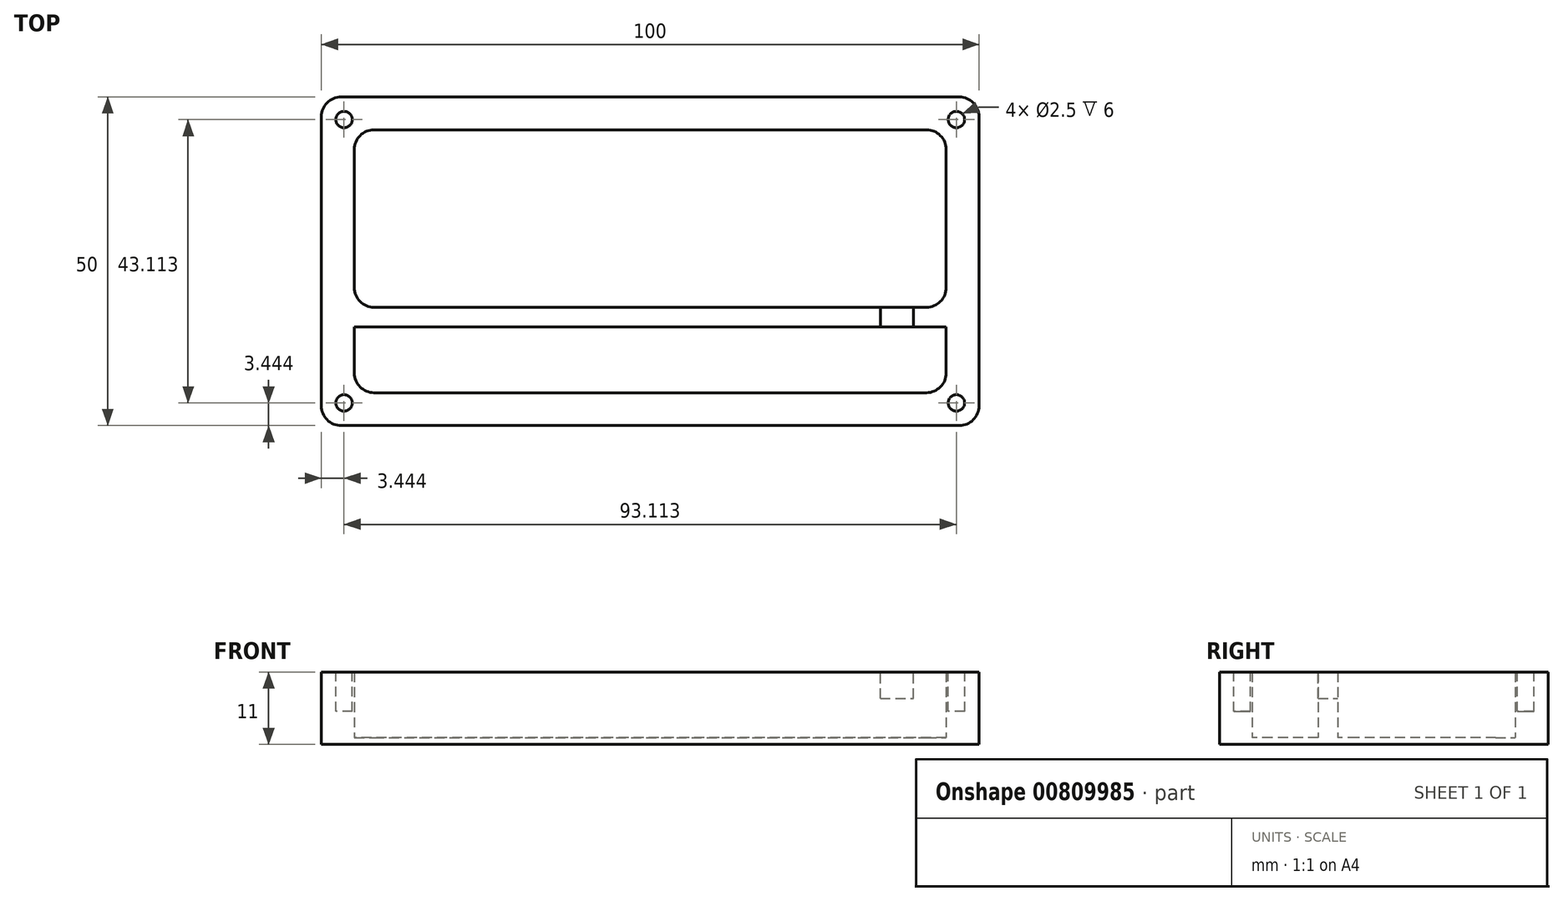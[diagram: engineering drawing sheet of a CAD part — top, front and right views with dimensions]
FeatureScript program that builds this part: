
annotation { "Feature Type Name" : "Feature", "Feature Type Description" : "" }
export const myFeature = defineFeature(function(context is Context, id is Id, definition is map)
    precondition{}
    {
        {
            var Q0;
            Q0=qCreatedBy(makeId("Top.planeOp"),FACE);
            var sketch = newSketch(context, id + "F0", { "sketchPlane" : qUnion([Q0])});
            skLineSegment(sketch, "E0.bottom", {"start": v(-50, -25) * mm, "end": v(50, -25) * mm});
            skLineSegment(sketch, "E0.top", {"start": v(-50, 25) * mm, "end": v(50, 25) * mm});
            skLineSegment(sketch, "E0.left", {"start": v(-50, -25) * mm, "end": v(-50, 25) * mm});
            skLineSegment(sketch, "E0.right", {"start": v(50, -25) * mm, "end": v(50, 25) * mm});
            skLineSegment(sketch, "E1", {"start": v(0, -25) * mm, "end": v(0, 74.13) * mm, "construction": true});
            skLineSegment(sketch, "E2", {"start": v(-150.25, 0) * mm, "end": v(50, 0) * mm, "construction": true});
            skSolve(sketch);
        }
        {
            var Q0;
            Q0 = qSketchRegion(id + "F0", true);
            extrude(context, id + "F1", {"entities" : qUnion([Q0]), "depth" : 1 * mm, "offsetDistance" : 25 * mm});
        }
        {
            var Q0;
            Q0=makeQuery(id+"F1.opExtrude","CAP_FACE",FACE,{"disambiguationData":[OSD([sQuery(id+"F0.wireOp",EDGE,"E0.bottom"),sQuery(id+"F0.wireOp",EDGE,"E0.top"),sQuery(id+"F0.wireOp",EDGE,"E0.left"),sQuery(id+"F0.wireOp",EDGE,"E0.right")])],"isStart":false});
            var sketch = newSketch(context, id + "F2", { "sketchPlane" : qUnion([Q0])});
            skLineSegment(sketch, "E3.bottom", {"start": v(-50, 25) * mm, "end": v(50, 25) * mm});
            skLineSegment(sketch, "E3.top", {"start": v(-50, -25) * mm, "end": v(50, -25) * mm});
            skLineSegment(sketch, "E3.left", {"start": v(-50, 25) * mm, "end": v(-50, -25) * mm});
            skLineSegment(sketch, "E3.right", {"start": v(50, 25) * mm, "end": v(50, -25) * mm});
            skLineSegment(sketch, "E4.bottom", {"start": v(-45, 20) * mm, "end": v(45, 20) * mm});
            skLineSegment(sketch, "E4.top", {"start": v(-45, -20) * mm, "end": v(45, -20) * mm});
            skLineSegment(sketch, "E4.left", {"start": v(-45, 20) * mm, "end": v(-45, -20) * mm});
            skLineSegment(sketch, "E4.right", {"start": v(45, 20) * mm, "end": v(45, -20) * mm});
            skSolve(sketch);
        }
        {
            var Q0;
            Q0=makeQuery(id+"F2.imprint","IMPRINT",FACE,{"disambiguationData":[TD([[makeQuery(id+"F2.imprint","IMPRINT",EDGE,{"derivedFrom":sQuery(id+"F2.wireOp",EDGE,"E3.bottom")}),-1.0]])]});
            var Q1;
            Q1 = qSketchRegion(id + "F2", true);
            extrude(context, id + "F3", {"entities" : qUnion([Q0, Q1]), "operationType" : NewBodyOperationType.ADD, "depth" : 10 * mm, "offsetDistance" : 25 * mm});
        }
        {
            var Q0;
            Q0=qCreatedBy(makeId("Top.planeOp"),FACE);
            var sketch = newSketch(context, id + "F4", { "sketchPlane" : qUnion([Q0])});
            skLineSegment(sketch, "E5.bottom", {"start": v(-45, -7) * mm, "end": v(45, -7) * mm});
            skLineSegment(sketch, "E5.top", {"start": v(-45, -10) * mm, "end": v(45, -10) * mm});
            skLineSegment(sketch, "E5.right", {"start": v(45, -7) * mm, "end": v(45, -10) * mm});
            skLineSegment(sketch, "E6", {"start": v(-45, -7) * mm, "end": v(-45, -10) * mm});
            skSolve(sketch);
        }
        {
            var Q0;
            Q0 = qSketchRegion(id + "F4", true);
            var Q1;
            Q1=makeQuery(id+"F3.opExtrude","CAP_FACE",FACE,{"disambiguationData":[OSD([sQuery(id+"F2.wireOp",EDGE,"E3.bottom"),sQuery(id+"F2.wireOp",EDGE,"E3.top"),sQuery(id+"F2.wireOp",EDGE,"E3.left"),sQuery(id+"F2.wireOp",EDGE,"E3.right"),sQuery(id+"F2.wireOp",EDGE,"E4.bottom"),sQuery(id+"F2.wireOp",EDGE,"E4.top"),sQuery(id+"F2.wireOp",EDGE,"E4.left"),sQuery(id+"F2.wireOp",EDGE,"E4.right")])],"isStart":false});
            extrude(context, id + "F5", {"entities" : qUnion([Q0]), "operationType" : NewBodyOperationType.ADD, "endBound" : BoundingType.UP_TO_SURFACE, "depth" : 25 * mm, "endBoundEntityFace" : qUnion([Q1]), "offsetDistance" : 25 * mm});
        }
        {
            var Q0;
            Q0=makeQuery(id+"F5.opExtrude","SWEPT_FACE",FACE,{"disambiguationData":[OSD([sQuery(id+"F4.wireOp",EDGE,"E5.bottom")])]});
            var sketch = newSketch(context, id + "F6", { "sketchPlane" : qUnion([Q0])});
            skLineSegment(sketch, "E7.bottom", {"start": v(-40, 11) * mm, "end": v(-35, 11) * mm});
            skLineSegment(sketch, "E7.top", {"start": v(-40, 7) * mm, "end": v(-35, 7) * mm});
            skLineSegment(sketch, "E7.left", {"start": v(-40, 11) * mm, "end": v(-40, 7) * mm});
            skLineSegment(sketch, "E7.right", {"start": v(-35, 11) * mm, "end": v(-35, 7) * mm});
            skSolve(sketch);
        }
        {
            var Q0;
            Q0 = qSketchRegion(id + "F6", true);
            extrude(context, id + "F7", {"entities" : qUnion([Q0]), "operationType" : NewBodyOperationType.REMOVE, "endBound" : BoundingType.UP_TO_NEXT, "oppositeDirection" : true, "depth" : 25 * mm, "offsetDistance" : 25 * mm});
        }
        {
            var Q0;
            Q0=makeQuery(id+"F3.boolean.opBoolean","MERGE",EDGE,{"derivedFrom":[makeQuery(id+"F1.opExtrude","SWEPT_EDGE",EDGE,{"disambiguationData":[OSD([sQuery(id+"F0.wireOp",EDGE,"E0.bottom"),sQuery(id+"F0.wireOp",EDGE,"E0.right")])]}),makeQuery(id+"F3.opExtrude","SWEPT_EDGE",EDGE,{"disambiguationData":[OSD([sQuery(id+"F2.wireOp",EDGE,"E3.top"),sQuery(id+"F2.wireOp",EDGE,"E3.right")])]})]});
            var Q1;
            Q1=makeQuery(id+"F3.boolean.opBoolean","MERGE",EDGE,{"derivedFrom":[makeQuery(id+"F1.opExtrude","SWEPT_EDGE",EDGE,{"disambiguationData":[OSD([sQuery(id+"F0.wireOp",EDGE,"E0.top"),sQuery(id+"F0.wireOp",EDGE,"E0.right")])]}),makeQuery(id+"F3.opExtrude","SWEPT_EDGE",EDGE,{"disambiguationData":[OSD([sQuery(id+"F2.wireOp",EDGE,"E3.bottom"),sQuery(id+"F2.wireOp",EDGE,"E3.right")])]})]});
            var Q2;
            Q2=makeQuery(id+"F3.boolean.opBoolean","MERGE",EDGE,{"derivedFrom":[makeQuery(id+"F1.opExtrude","SWEPT_EDGE",EDGE,{"disambiguationData":[OSD([sQuery(id+"F0.wireOp",EDGE,"E0.bottom"),sQuery(id+"F0.wireOp",EDGE,"E0.left")])]}),makeQuery(id+"F3.opExtrude","SWEPT_EDGE",EDGE,{"disambiguationData":[OSD([sQuery(id+"F2.wireOp",EDGE,"E3.top"),sQuery(id+"F2.wireOp",EDGE,"E3.left")])]})]});
            var Q3;
            Q3=makeQuery(id+"F3.boolean.opBoolean","MERGE",EDGE,{"derivedFrom":[makeQuery(id+"F1.opExtrude","SWEPT_EDGE",EDGE,{"disambiguationData":[OSD([sQuery(id+"F0.wireOp",EDGE,"E0.top"),sQuery(id+"F0.wireOp",EDGE,"E0.left")])]}),makeQuery(id+"F3.opExtrude","SWEPT_EDGE",EDGE,{"disambiguationData":[OSD([sQuery(id+"F2.wireOp",EDGE,"E3.bottom"),sQuery(id+"F2.wireOp",EDGE,"E3.left")])]})]});
            var Q4;
            Q4=makeQuery(id+"F3.opExtrude","SWEPT_EDGE",EDGE,{"disambiguationData":[OSD([sQuery(id+"F2.wireOp",EDGE,"E4.top"),sQuery(id+"F2.wireOp",EDGE,"E4.right")])]});
            var Q5;
            Q5=makeQuery(id+"F3.opExtrude","SWEPT_EDGE",EDGE,{"disambiguationData":[OSD([sQuery(id+"F2.wireOp",EDGE,"E4.top"),sQuery(id+"F2.wireOp",EDGE,"E4.left")])]});
            var Q6;
            Q6=makeQuery(id+"F3.opExtrude","SWEPT_EDGE",EDGE,{"disambiguationData":[OSD([sQuery(id+"F2.wireOp",EDGE,"E4.bottom"),sQuery(id+"F2.wireOp",EDGE,"E4.right")])]});
            var Q7;
            Q7=makeQuery(id+"F3.opExtrude","SWEPT_EDGE",EDGE,{"disambiguationData":[OSD([sQuery(id+"F2.wireOp",EDGE,"E4.bottom"),sQuery(id+"F2.wireOp",EDGE,"E4.left")])]});
            var Q8;
            Q8=makeQuery(id+"F5.opExtrude","SWEPT_EDGE",EDGE,{"disambiguationData":[OSD([sQuery(id+"F4.wireOp",EDGE,"E5.bottom"),sQuery(id+"F4.wireOp",EDGE,"E5.right")])]});
            var Q9;
            Q9=makeQuery(id+"F5.opExtrude","SWEPT_EDGE",EDGE,{"disambiguationData":[OSD([sQuery(id+"F4.wireOp",EDGE,"E5.bottom"),sQuery(id+"F4.wireOp",EDGE,"E6")])]});
            var Q10;
            Q10=makeQuery(id+"F5.opExtrude","SWEPT_EDGE",EDGE,{"disambiguationData":[OSD([sQuery(id+"F4.wireOp",EDGE,"E5.top"),sQuery(id+"F4.wireOp",EDGE,"E5.right")])]});
            var Q11;
            Q11=makeQuery(id+"F5.opExtrude","SWEPT_EDGE",EDGE,{"disambiguationData":[OSD([sQuery(id+"F4.wireOp",EDGE,"E5.top"),sQuery(id+"F4.wireOp",EDGE,"E6")])]});
            fillet(context, id + "F8", {"entities" : qUnion([Q0, Q1, Q2, Q3, Q4, Q5, Q6, Q7, Q8, Q9, Q10, Q11]), "radius" : 3 * mm, "tangentPropagation" : true, "allowEdgeOverflow" : false});
        }
        {
            var Q0;
            {var subQ0=sQuery(id+"F2.wireOp",EDGE,"E4.right");var subQ1=sQuery(id+"F2.wireOp",EDGE,"E4.left");var subQ2=sQuery(id+"F2.wireOp",EDGE,"E4.top");var subQ3=sQuery(id+"F2.wireOp",EDGE,"E4.bottom");var subQ4=sQuery(id+"F2.wireOp",EDGE,"E3.right");var subQ5=sQuery(id+"F2.wireOp",EDGE,"E3.left");var subQ6=sQuery(id+"F2.wireOp",EDGE,"E3.top");var subQ7=sQuery(id+"F2.wireOp",EDGE,"E3.bottom");Q0=makeQuery(id+"F5.boolean.opBoolean","MERGE",FACE,{"derivedFrom":[makeQuery(id+"F3.opExtrude","CAP_FACE",FACE,{"disambiguationData":[OSD([subQ7,subQ6,subQ5,subQ4,subQ3,subQ2,subQ1,subQ0])],"isStart":false}),makeQuery(id+"F5.opExtrude","CAP_FACE",FACE,{"disambiguationData":[OSD([subQ7,subQ6,subQ5,subQ4,subQ3,subQ2,subQ1,subQ0])],"isStart":false})]});}
            var sketch = newSketch(context, id + "F9", { "sketchPlane" : qUnion([Q0])});
            skLineSegment(sketch, "E8", {"start": v(0, 26.64) * mm, "end": v(0, -27.57) * mm, "construction": true});
            skLineSegment(sketch, "E9", {"start": v(-50.8, 0) * mm, "end": v(56.22, 0) * mm, "construction": true});
            skCircle(sketch, "E10", {"center": v(46.56, -21.56) * mm, "radius": 1.25 * mm});
            skLineSegment(sketch, "E11", {"start": v(49.12, -24.12) * mm, "end": v(44.12, -19.12) * mm, "construction": true});
            skLineSegment(sketch, "E12", {"start": v(46.56, -21.56) * mm, "end": v(46.56, -25) * mm});
            skLineSegment(sketch, "E13", {"start": v(46.56, -21.56) * mm, "end": v(44.12, -19.12) * mm});
            skCircle(sketch, "E14.MirrorC", {"center": v(-46.56, -21.56) * mm, "radius": 1.25 * mm});
            skCircle(sketch, "E15.MirrorC", {"center": v(-46.56, 21.56) * mm, "radius": 1.25 * mm});
            skCircle(sketch, "E16.MirrorC", {"center": v(46.56, 21.56) * mm, "radius": 1.25 * mm});
            skSolve(sketch);
        }
        {
            var Q0;
            Q0 = qSketchRegion(id + "F9", true);
            extrude(context, id + "F10", {"entities" : qUnion([Q0]), "operationType" : NewBodyOperationType.REMOVE, "oppositeDirection" : true, "depth" : 6 * mm, "offsetDistance" : 25 * mm});
        }
    });
